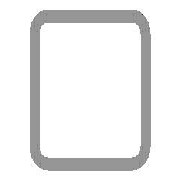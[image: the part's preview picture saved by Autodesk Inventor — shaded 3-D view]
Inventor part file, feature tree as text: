
AUTODESK INVENTOR PART (.ipt)
format: ipt  version: 2025.3 (Build 293356030, 356C)  size: 129,024 bytes
history: native  units: mm (DEFAULTED — no unit token found)
features: other x3, sketch x1, plane x1
ambient origin geometry x8: Origin, YZ Plane, XZ Plane, XY Plane, X Axis, Y Axis, Z Axis, Center Point
bodies: Solid1 (feature_tree), Body (feature_tree)
feature tree (5):
  other  "Driven Length"
  other  "Start plane"
  other  "End plane"
  sketch  "Sketch3"  dims[d3=2200.0mm d4=0.0mm d7=4.0mm d9=40.0mm d11=40.0mm d12=2.0mm d13=-0.0mm d14=2200.0mm d15=20.0mm d16=20.0mm d17=90.0deg d18=2200.0mm]
  plane  "Work Plane3"
